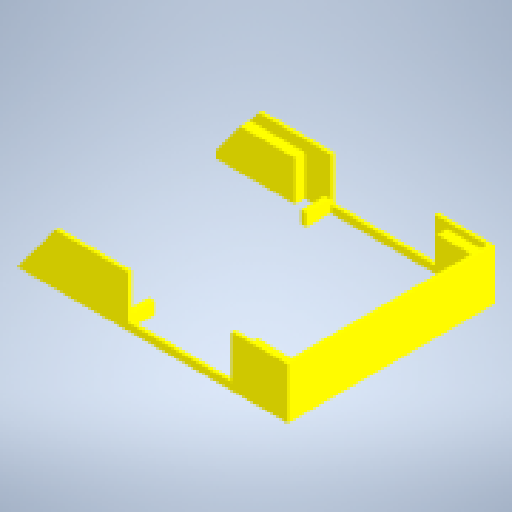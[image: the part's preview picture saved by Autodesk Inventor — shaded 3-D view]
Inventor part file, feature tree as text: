
AUTODESK INVENTOR PART (.ipt)
format: ipt  version: 2024 (Build 280153000, 153)  size: 789,504 bytes
history: native  units: mm
features: extrude x22, sketch x21, mirror x6
ambient origin geometry x8: Origin, YZ Plane, XZ Plane, XY Plane, X Axis, Y Axis, Z Axis, Center Point
bodies: Solid1 (feature_tree)
feature tree (49):
  extrude  "Extrusion1"  Depth=100.0mm
  sketch  "Sketch2"  dims[d2=3.125mm d3=0.0mm d4=20.0mm]
  extrude  "Extrusion2"  Depth=20.0mm
  extrude  "Extrusion3"  Depth=15.0mm
  extrude  "Extrusion4"  Depth=10.0mm TaperAngle=0.0deg
  extrude  "Extrusion5"  Depth=7.0mm TaperAngle=0.0deg
  extrude  "Extrusion6"  Depth=6.0mm
  extrude  "Extrusion7"  Depth=1.3mm
  extrude  "Extrusion8"  Depth=2.0mm
  extrude  "Extrusion9"  Depth=1.3mm TaperAngle=0.0deg
  extrude  "Extrusion10"  Depth=2.0mm TaperAngle=0.0deg
  extrude  "Extrusion11"  Depth=5.0mm
  mirror  "Mirror1"
  extrude  "Extrusion12"  Depth=5.0mm
  extrude  "Extrusion13"  Depth=22.4mm TaperAngle=0.0deg
  mirror  "Mirror2"
  extrude  "Extrusion14"  Depth=15.0mm TaperAngle=0.0deg
  mirror  "Mirror3"
  extrude  "Extrusion15"  Depth=20.0mm
  mirror  "Mirror4"
  extrude  "Extrusion16"  Depth=3.0mm TaperAngle=0.0deg
  mirror  "Mirror5"
  extrude  "Extrusion19"  Depth=12.0mm
  extrude  "Extrusion20"  Depth=20.0mm
  extrude  "Extrusion26"  Depth=20.0mm TaperAngle=0.0deg
  extrude  "Extrusion27"  Depth=20.0mm TaperAngle=0.0deg
  extrude  "Extrusion28"  Depth=0.5mm TaperAngle=0.0deg
  extrude  "Extrusion31"  Depth=0.5mm TaperAngle=0.0deg
  mirror  "Mirror6"
  sketch  "Sketch1"  dims[d0=170.0mm d1=100.0mm]
  sketch  "Sketch3"  dims[d5=20.0mm d6=15.0mm]
  sketch  "Sketch4"  dims[d7=22.4mm d8=0.0mm d9=10.0mm d10=0.0mm]
  sketch  "Sketch5"  dims[d11=6.0mm d12=7.0mm d13=0.0mm]
  sketch  "Sketch6"  dims[d14=20.0mm d15=20.0mm d16=15.0mm d17=6.0mm]
  sketch  "Sketch7"  dims[d18=7.0mm d19=0.0mm d20=1.3mm]
  sketch  "Sketch8"  dims[d21=1.3mm d22=2.0mm]
  sketch  "Sketch9"  dims[d23=25.525mm d24=0.0mm d25=1.3mm d26=0.0mm]
  sketch  "Sketch10"  dims[d27=1.3mm d28=0.0mm d29=2.0mm d30=0.0mm]
  sketch  "Sketch11"  dims[d31=20.0mm d32=5.0mm]
  sketch  "Sketch12"  dims[d33=20.0mm d34=5.0mm]
  sketch  "Sketch13"  dims[d35=22.4mm d36=0.0mm d37=27.4mm d38=0.0mm]
  sketch  "Sketch14"  dims[d39=7.0mm d40=15.0mm d41=0.0mm]
  sketch  "Sketch15"  dims[d42=19.5mm d43=20.0mm]
  sketch  "Sketch17"  dims[d44=2.0mm d45=3.0mm d46=0.0mm]
  sketch  "Sketch18"  dims[d47=3.0mm d48=12.0mm]
  sketch  "Sketch24"  dims[d49=6.0mm d50=0.0mm d51=20.0mm]
  sketch  "Sketch25"  dims[d52=5.0mm d53=20.0mm d54=0.0mm]
  sketch  "Sketch26"  dims[d55=20.0mm d56=0.0mm d64=0.922mm d65=0.0mm]
  sketch  "Sketch29"  dims[d66=125.922mm d67=0.0mm d78=19.25mm d79=0.0mm d80=19.25mm d81=0.0mm d82=133.0mm d83=0.0mm d88=0.5mm d89=0.0mm d68=0.5mm d69=0.872665mm]
